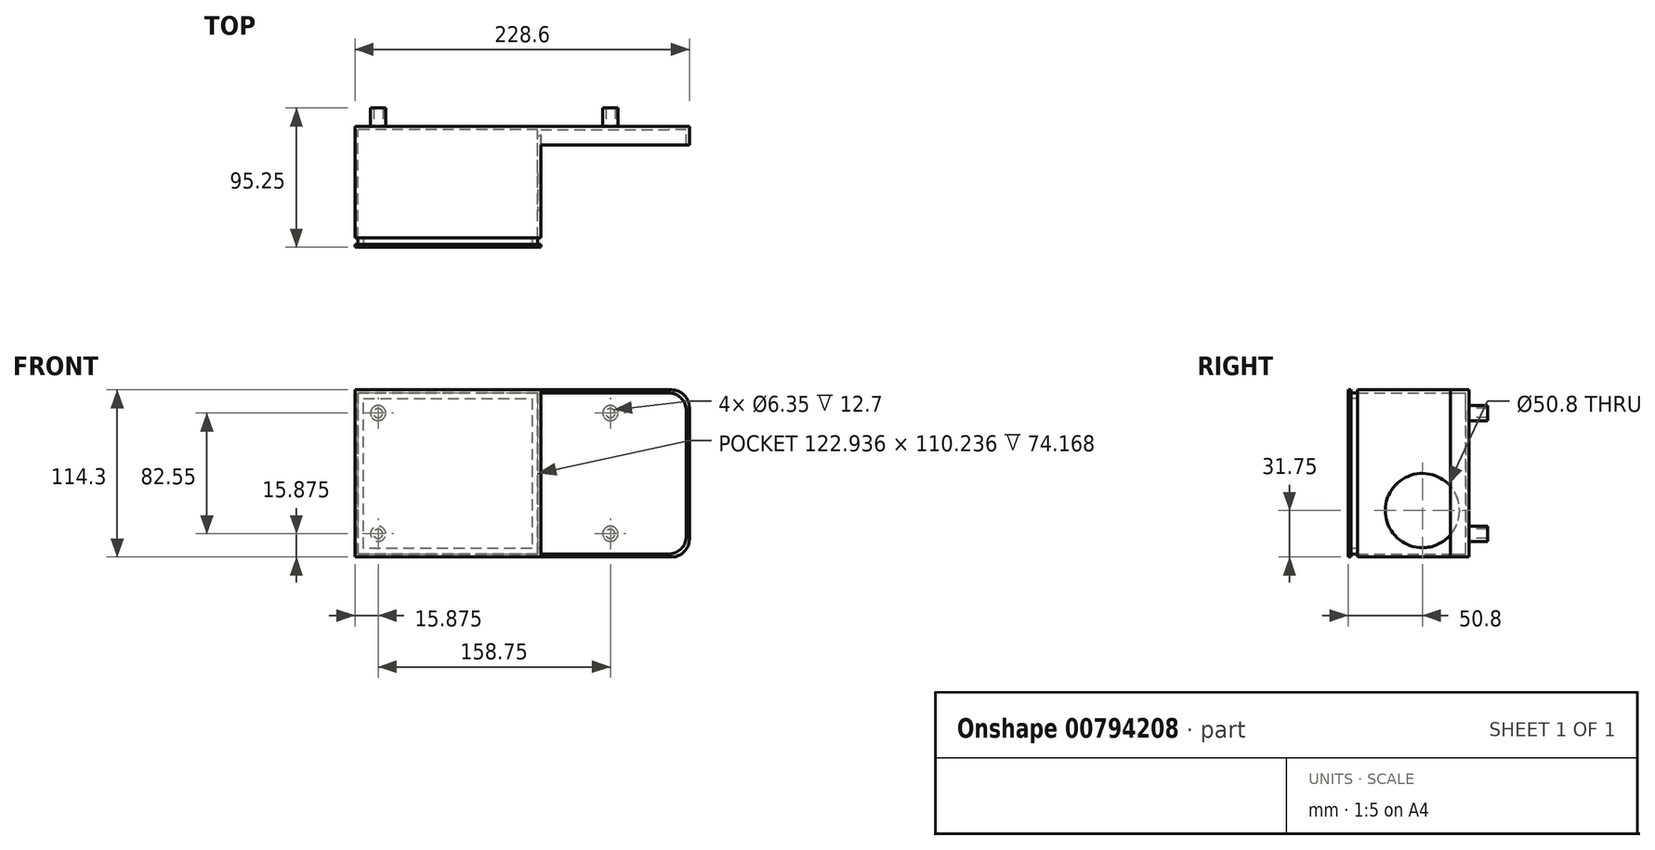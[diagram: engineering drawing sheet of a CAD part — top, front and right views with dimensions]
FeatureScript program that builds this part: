
annotation { "Feature Type Name" : "Feature", "Feature Type Description" : "" }
export const myFeature = defineFeature(function(context is Context, id is Id, definition is map)
    precondition{}
    {
        {
            var Q0;
            Q0=qCreatedBy(makeId("Front.planeOp"),FACE);
            var sketch = newSketch(context, id + "F0", { "sketchPlane" : qUnion([Q0])});
            skLineSegment(sketch, "E0", {"start": v(-127, 114.3) * mm, "end": v(-127, 0) * mm});
            skLineSegment(sketch, "E1", {"start": v(-127, 0) * mm, "end": v(0, 0) * mm});
            skLineSegment(sketch, "E2", {"start": v(0, 0) * mm, "end": v(0, 114.3) * mm});
            skLineSegment(sketch, "E3", {"start": v(0, 114.3) * mm, "end": v(-127, 114.3) * mm});
            skLineSegment(sketch, "E4.0", {"start": v(-2.03, 112.27) * mm, "end": v(-124.97, 112.27) * mm});
            skLineSegment(sketch, "E4.1", {"start": v(-2.03, 2.03) * mm, "end": v(-2.03, 112.27) * mm});
            skLineSegment(sketch, "E4.2", {"start": v(-124.97, 2.03) * mm, "end": v(-2.03, 2.03) * mm});
            skLineSegment(sketch, "E4.3", {"start": v(-124.97, 112.27) * mm, "end": v(-124.97, 2.03) * mm});
            skLineSegment(sketch, "E5", {"start": v(0, 0) * mm, "end": v(101.6, 0) * mm});
            skLineSegment(sketch, "E6", {"start": v(101.6, 0) * mm, "end": v(101.6, 114.3) * mm});
            skLineSegment(sketch, "E7", {"start": v(101.6, 114.3) * mm, "end": v(0, 114.3) * mm});
            skLineSegment(sketch, "E8.0", {"start": v(99.57, 112.27) * mm, "end": v(0, 112.27) * mm});
            skLineSegment(sketch, "E8.1", {"start": v(99.57, 2.03) * mm, "end": v(99.57, 112.27) * mm});
            skLineSegment(sketch, "E8.2", {"start": v(0, 2.03) * mm, "end": v(99.57, 2.03) * mm});
            skSolve(sketch);
        }
        {
            var Q0;
            Q0=makeQuery(id+"F0.imprint","IMPRINT",FACE,{"disambiguationData":[TD([[makeQuery(id+"F0.imprint","IMPRINT",EDGE,{"derivedFrom":sQuery(id+"F0.wireOp",EDGE,"E0")}),1.0]])]});
            extrude(context, id + "F1", {"entities" : qUnion([Q0]), "depth" : 76.2 * mm, "offsetDistance" : 25.4 * mm});
        }
        {
            var Q0;
            Q0=makeQuery(id+"F0.imprint","IMPRINT",FACE,{"disambiguationData":[TD([[makeQuery(id+"F0.imprint","IMPRINT",EDGE,{"derivedFrom":sQuery(id+"F0.wireOp",EDGE,"E4.0")}),1.0]])]});
            extrude(context, id + "F2", {"entities" : qUnion([Q0]), "operationType" : NewBodyOperationType.ADD, "depth" : 2.03 * mm, "offsetDistance" : 25.4 * mm});
        }
        {
            var Q0;
            Q0=makeQuery(id+"F1.opExtrude","SWEPT_FACE",FACE,{"disambiguationData":[OSD([sQuery(id+"F0.wireOp",EDGE,"E2")])]});
            var sketch = newSketch(context, id + "F3", { "sketchPlane" : qUnion([Q0])});
            skCircle(sketch, "E9", {"center": v(-31.75, 31.75) * mm, "radius": 25.4 * mm});
            skSolve(sketch);
        }
        {
            var Q0;
            Q0=qCreatedBy(makeId("Front.planeOp"),FACE);
            cPlane(context, id + "F4", {"entities" : qUnion([Q0]), "cplaneType" : CPlaneType.OFFSET, "offset" : 82.55 * mm, "width" : 152.4 * mm, "height" : 152.4 * mm});
        }
        {
            var Q0;
            Q0=qCreatedBy(id+"F4.planeOp",FACE);
            var sketch = newSketch(context, id + "F5", { "sketchPlane" : qUnion([Q0])});
            skLineSegment(sketch, "E10", {"start": v(0, 0) * mm, "end": v(-127, 0) * mm});
            skLineSegment(sketch, "E11", {"start": v(-127, 0) * mm, "end": v(-127, 114.3) * mm});
            skLineSegment(sketch, "E12", {"start": v(-127, 114.3) * mm, "end": v(0, 114.3) * mm});
            skLineSegment(sketch, "E13", {"start": v(0, 114.3) * mm, "end": v(0, 0) * mm});
            skLineSegment(sketch, "E14.0", {"start": v(-124.84, 2.16) * mm, "end": v(-124.84, 112.14) * mm});
            skLineSegment(sketch, "E14.1", {"start": v(-2.16, 2.16) * mm, "end": v(-124.84, 2.16) * mm});
            skLineSegment(sketch, "E14.2", {"start": v(-2.16, 112.14) * mm, "end": v(-2.16, 2.16) * mm});
            skLineSegment(sketch, "E14.3", {"start": v(-124.84, 112.14) * mm, "end": v(-2.16, 112.14) * mm});
            skLineSegment(sketch, "E15.0", {"start": v(-121.03, 108.33) * mm, "end": v(-5.97, 108.33) * mm});
            skLineSegment(sketch, "E15.1", {"start": v(-121.03, 5.97) * mm, "end": v(-121.03, 108.33) * mm});
            skLineSegment(sketch, "E15.2", {"start": v(-5.97, 5.97) * mm, "end": v(-121.03, 5.97) * mm});
            skLineSegment(sketch, "E15.3", {"start": v(-5.97, 108.33) * mm, "end": v(-5.97, 5.97) * mm});
            skSolve(sketch);
        }
        {
            var Q0;
            Q0=makeQuery(id+"F5.imprint","IMPRINT",FACE,{"disambiguationData":[TD([[makeQuery(id+"F5.imprint","IMPRINT",EDGE,{"derivedFrom":sQuery(id+"F5.wireOp",EDGE,"E15.0")}),-1.0]])]});
            var Q1;
            Q1=makeQuery(id+"F5.imprint","IMPRINT",FACE,{"disambiguationData":[TD([[makeQuery(id+"F5.imprint","IMPRINT",EDGE,{"derivedFrom":sQuery(id+"F5.wireOp",EDGE,"E14.0")}),-1.0]])]});
            var Q2;
            Q2=makeQuery(id+"F5.imprint","IMPRINT",FACE,{"disambiguationData":[TD([[makeQuery(id+"F5.imprint","IMPRINT",EDGE,{"derivedFrom":sQuery(id+"F5.wireOp",EDGE,"E10")}),-1.0]])]});
            extrude(context, id + "F6", {"entities" : qUnion([Q0, Q1, Q2]), "oppositeDirection" : true, "depth" : 2.03 * mm, "offsetDistance" : 25.4 * mm});
        }
        {
            var Q0;
            Q0=makeQuery(id+"F5.imprint","IMPRINT",FACE,{"disambiguationData":[TD([[makeQuery(id+"F5.imprint","IMPRINT",EDGE,{"derivedFrom":sQuery(id+"F5.wireOp",EDGE,"E14.0")}),-1.0]])]});
            extrude(context, id + "F7", {"entities" : qUnion([Q0]), "operationType" : NewBodyOperationType.ADD, "oppositeDirection" : true, "depth" : 6.35 * mm, "offsetDistance" : 25.4 * mm});
        }
        {
            var Q0;
            {var subQ0=sQuery(id+"F0.wireOp",EDGE,"E8.0");Q0=makeQuery(id+"F0.imprint","IMPRINT",FACE,{"disambiguationData":[TD([[makeQuery(id+"F0.imprint","IMPRINT",EDGE,{"derivedFrom":subQ0}),1.0]])]});}
            var Q1;
            {var subQ0=sQuery(id+"F0.wireOp",EDGE,"E5");Q1=makeQuery(id+"F0.imprint","IMPRINT",FACE,{"disambiguationData":[TD([[makeQuery(id+"F0.imprint","IMPRINT",EDGE,{"derivedFrom":subQ0}),1.0]])]});}
            extrude(context, id + "F8", {"entities" : qUnion([Q0, Q1]), "operationType" : NewBodyOperationType.ADD, "depth" : 2.03 * mm, "offsetDistance" : 25.4 * mm});
        }
        {
            var Q0;
            {var subQ0=sQuery(id+"F0.wireOp",EDGE,"E5");Q0=makeQuery(id+"F0.imprint","IMPRINT",FACE,{"disambiguationData":[TD([[makeQuery(id+"F0.imprint","IMPRINT",EDGE,{"derivedFrom":subQ0}),1.0]])]});}
            extrude(context, id + "F9", {"entities" : qUnion([Q0]), "operationType" : NewBodyOperationType.ADD, "depth" : 12.7 * mm, "offsetDistance" : 25.4 * mm});
        }
        {
            var Q0;
            Q0 = qSketchRegion(id + "F3", true);
            extrude(context, id + "F10", {"entities" : qUnion([Q0]), "operationType" : NewBodyOperationType.REMOVE, "oppositeDirection" : true, "depth" : 6.35 * mm, "offsetDistance" : 25.4 * mm});
        }
        {
            var Q0;
            {var subQ0=sQuery(id+"F0.wireOp",EDGE,"E6");var subQ1=sQuery(id+"F0.wireOp",EDGE,"E5");Q0=makeQuery(id+"F9.boolean.opBoolean","MERGE",EDGE,{"derivedFrom":[makeQuery(id+"F8.opExtrude","SWEPT_EDGE",EDGE,{"disambiguationData":[OSD([subQ1,subQ0])]}),makeQuery(id+"F9.opExtrude","SWEPT_EDGE",EDGE,{"disambiguationData":[OSD([subQ1,subQ0])]})]});}
            var Q1;
            Q1=makeQuery(id+"F9.opExtrude","SWEPT_EDGE",EDGE,{"disambiguationData":[OSD([sQuery(id+"F0.wireOp",EDGE,"E8.1"),sQuery(id+"F0.wireOp",EDGE,"E8.2")])]});
            var Q2;
            Q2=makeQuery(id+"F9.opExtrude","SWEPT_EDGE",EDGE,{"disambiguationData":[OSD([sQuery(id+"F0.wireOp",EDGE,"E8.0"),sQuery(id+"F0.wireOp",EDGE,"E8.1")])]});
            var Q3;
            {var subQ0=sQuery(id+"F0.wireOp",EDGE,"E7");var subQ1=sQuery(id+"F0.wireOp",EDGE,"E6");Q3=makeQuery(id+"F9.boolean.opBoolean","MERGE",EDGE,{"derivedFrom":[makeQuery(id+"F8.opExtrude","SWEPT_EDGE",EDGE,{"disambiguationData":[OSD([subQ1,subQ0])]}),makeQuery(id+"F9.opExtrude","SWEPT_EDGE",EDGE,{"disambiguationData":[OSD([subQ1,subQ0])]})]});}
            fillet(context, id + "F11", {"entities" : qUnion([Q0, Q1, Q2, Q3]), "radius" : 12.26 * mm, "tangentPropagation" : true, "allowEdgeOverflow" : false});
        }
        {
            var Q0;
            {var subQ0=sQuery(id+"F0.wireOp",EDGE,"E2");var subQ1=sQuery(id+"F0.wireOp",EDGE,"E4.3");var subQ2=sQuery(id+"F0.wireOp",EDGE,"E4.2");var subQ3=sQuery(id+"F0.wireOp",EDGE,"E4.1");var subQ4=sQuery(id+"F0.wireOp",EDGE,"E4.0");Q0=makeQuery(id+"F8.boolean.opBoolean","MERGE",FACE,{"derivedFrom":[makeQuery(id+"F2.boolean.opBoolean","MERGE",FACE,{"derivedFrom":[makeQuery(id+"F1.opExtrude","CAP_FACE",FACE,{"disambiguationData":[OSD([sQuery(id+"F0.wireOp",EDGE,"E0"),sQuery(id+"F0.wireOp",EDGE,"E1"),subQ0,sQuery(id+"F0.wireOp",EDGE,"E3"),subQ4,subQ3,subQ2,subQ1])],"isStart":true}),makeQuery(id+"F2.opExtrude","CAP_FACE",FACE,{"disambiguationData":[OSD([subQ4,subQ3,subQ2,subQ1])],"isStart":true})]}),makeQuery(id+"F8.opExtrude","CAP_FACE",FACE,{"disambiguationData":[OSD([subQ0,sQuery(id+"F0.wireOp",EDGE,"E5"),sQuery(id+"F0.wireOp",EDGE,"E6"),sQuery(id+"F0.wireOp",EDGE,"E7")])],"isStart":true})]});}
            var sketch = newSketch(context, id + "F12", { "sketchPlane" : qUnion([Q0])});
            skCircle(sketch, "E16", {"center": v(111.12, 15.88) * mm, "radius": 3.18 * mm});
            skCircle(sketch, "E17", {"center": v(111.12, 98.42) * mm, "radius": 3.18 * mm});
            skCircle(sketch, "E18", {"center": v(-47.63, 98.43) * mm, "radius": 3.18 * mm});
            skCircle(sketch, "E19", {"center": v(-47.63, 15.88) * mm, "radius": 3.18 * mm});
            skCircle(sketch, "E20.0", {"center": v(-47.63, 98.43) * mm, "radius": 5.2 * mm});
            skArc(sketch, "E21.0", {"start": v(-89.34, 107.95) * mm, "mid": v(-93.52, 106.22) * mm, "end": v(-95.25, 102.04) * mm});
            skArc(sketch, "E21.1", {"start": v(-95.25, 12.26) * mm, "mid": v(-93.52, 8.08) * mm, "end": v(-89.34, 6.35) * mm});
            skLineSegment(sketch, "E21.2", {"start": v(-89.34, 6.35) * mm, "end": v(120.65, 6.35) * mm});
            skLineSegment(sketch, "E21.3", {"start": v(-95.25, 102.04) * mm, "end": v(-95.25, 12.26) * mm});
            skLineSegment(sketch, "E21.4", {"start": v(120.65, 6.35) * mm, "end": v(120.65, 107.95) * mm});
            skLineSegment(sketch, "E21.5", {"start": v(120.65, 107.95) * mm, "end": v(-89.34, 107.95) * mm});
            skCircle(sketch, "E22.0", {"center": v(-47.63, 15.88) * mm, "radius": 5.2 * mm});
            skCircle(sketch, "E23.0", {"center": v(111.12, 98.42) * mm, "radius": 5.2 * mm});
            skCircle(sketch, "E24.0", {"center": v(111.12, 15.88) * mm, "radius": 5.2 * mm});
            skSolve(sketch);
        }
        {
            var Q0;
            Q0=makeQuery(id+"F12.imprint","IMPRINT",FACE,{"disambiguationData":[TD([[makeQuery(id+"F12.imprint","IMPRINT",EDGE,{"derivedFrom":sQuery(id+"F12.wireOp",EDGE,"E16")}),-1.0]])]});
            var Q1;
            Q1=makeQuery(id+"F12.imprint","IMPRINT",FACE,{"disambiguationData":[TD([[makeQuery(id+"F12.imprint","IMPRINT",EDGE,{"derivedFrom":sQuery(id+"F12.wireOp",EDGE,"E17")}),-1.0]])]});
            var Q2;
            Q2=makeQuery(id+"F12.imprint","IMPRINT",FACE,{"disambiguationData":[TD([[makeQuery(id+"F12.imprint","IMPRINT",EDGE,{"derivedFrom":sQuery(id+"F12.wireOp",EDGE,"E18")}),-1.0]])]});
            var Q3;
            Q3=makeQuery(id+"F12.imprint","IMPRINT",FACE,{"disambiguationData":[TD([[makeQuery(id+"F12.imprint","IMPRINT",EDGE,{"derivedFrom":sQuery(id+"F12.wireOp",EDGE,"E19")}),-1.0]])]});
            extrude(context, id + "F13", {"entities" : qUnion([Q0, Q1, Q2, Q3]), "operationType" : NewBodyOperationType.ADD, "depth" : 12.7 * mm, "offsetDistance" : 25.4 * mm});
        }
    });
